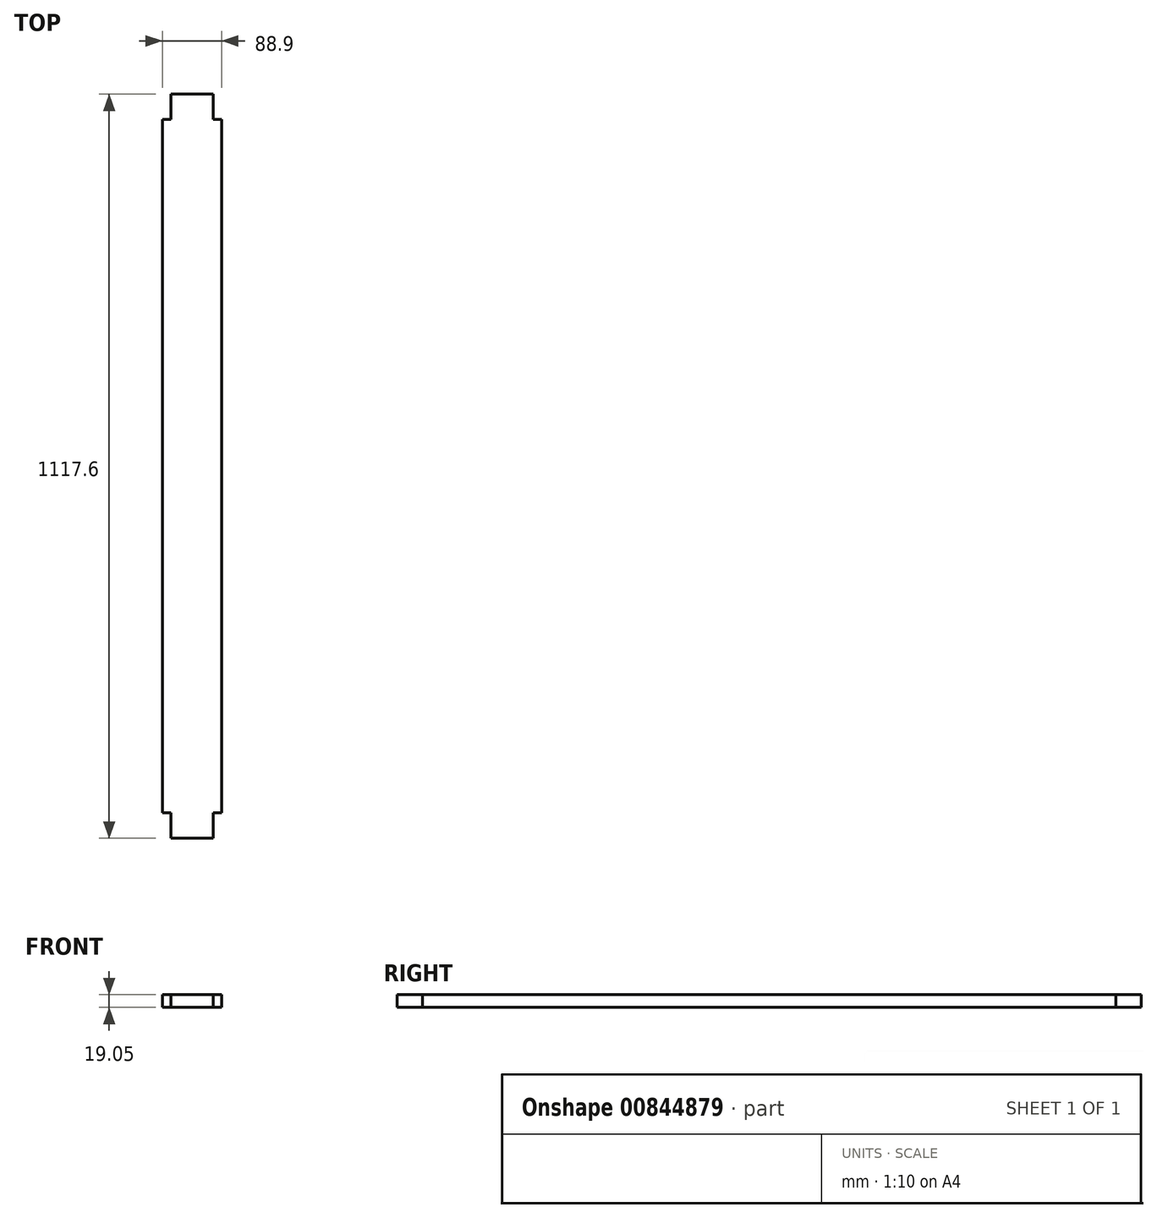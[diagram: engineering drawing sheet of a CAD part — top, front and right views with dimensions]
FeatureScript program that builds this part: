
annotation { "Feature Type Name" : "Feature", "Feature Type Description" : "" }
export const myFeature = defineFeature(function(context is Context, id is Id, definition is map)
    precondition{}
    {
        {
            var Q0;
            Q0=qCreatedBy(makeId("Front.planeOp"),FACE);
            var sketch = newSketch(context, id + "F0", { "sketchPlane" : qUnion([Q0])});
            skLineSegment(sketch, "E0.bottom", {"start": v(0, 0) * mm, "end": v(88.9, 0) * mm});
            skLineSegment(sketch, "E0.top", {"start": v(0, 19.05) * mm, "end": v(88.9, 19.05) * mm});
            skLineSegment(sketch, "E0.left", {"start": v(0, 0) * mm, "end": v(0, 19.05) * mm});
            skLineSegment(sketch, "E0.right", {"start": v(88.9, 0) * mm, "end": v(88.9, 19.05) * mm});
            skSolve(sketch);
        }
        {
            var Q0;
            Q0=makeQuery(id+"F0.imprint","IMPRINT",FACE,{"disambiguationData":[TD([[makeQuery(id+"F0.imprint","IMPRINT",EDGE,{"derivedFrom":sQuery(id+"F0.wireOp",EDGE,"E0.bottom")}),1.0]])]});
            extrude(context, id + "F1", {"entities" : qUnion([Q0]), "oppositeDirection" : true, "depth" : 1041.4 * mm, "offsetDistance" : 25.4 * mm});
        }
        {
            var Q0;
            Q0=makeQuery(id+"F1.opExtrude","CAP_FACE",FACE,{"disambiguationData":[OSD([sQuery(id+"F0.wireOp",EDGE,"E0.bottom"),sQuery(id+"F0.wireOp",EDGE,"E0.top"),sQuery(id+"F0.wireOp",EDGE,"E0.left"),sQuery(id+"F0.wireOp",EDGE,"E0.right")])],"isStart":true});
            var sketch = newSketch(context, id + "F2", { "sketchPlane" : qUnion([Q0])});
            skLineSegment(sketch, "E1.bottom", {"start": v(12.7, 0) * mm, "end": v(76.2, 0) * mm});
            skLineSegment(sketch, "E1.top", {"start": v(12.7, 19.05) * mm, "end": v(76.2, 19.05) * mm});
            skLineSegment(sketch, "E1.left", {"start": v(12.7, 0) * mm, "end": v(12.7, 19.05) * mm});
            skLineSegment(sketch, "E1.right", {"start": v(76.2, 0) * mm, "end": v(76.2, 19.05) * mm});
            skSolve(sketch);
        }
        {
            var Q0;
            Q0=makeQuery(id+"F2.imprint","IMPRINT",FACE,{"disambiguationData":[TD([[makeQuery(id+"F2.imprint","IMPRINT",EDGE,{"derivedFrom":sQuery(id+"F2.wireOp",EDGE,"E1.bottom")}),1.0]])]});
            extrude(context, id + "F3", {"entities" : qUnion([Q0]), "operationType" : NewBodyOperationType.ADD, "depth" : 38.1 * mm, "offsetDistance" : 25.4 * mm});
        }
        {
            var Q0;
            Q0=makeQuery(id+"F1.opExtrude","CAP_FACE",FACE,{"disambiguationData":[OSD([sQuery(id+"F0.wireOp",EDGE,"E0.bottom"),sQuery(id+"F0.wireOp",EDGE,"E0.top"),sQuery(id+"F0.wireOp",EDGE,"E0.left"),sQuery(id+"F0.wireOp",EDGE,"E0.right")])],"isStart":false});
            var sketch = newSketch(context, id + "F4", { "sketchPlane" : qUnion([Q0])});
            skLineSegment(sketch, "E2.bottom", {"start": v(-76.2, 19.05) * mm, "end": v(-12.7, 19.05) * mm});
            skLineSegment(sketch, "E2.top", {"start": v(-76.2, 0) * mm, "end": v(-12.7, 0) * mm});
            skLineSegment(sketch, "E2.left", {"start": v(-76.2, 19.05) * mm, "end": v(-76.2, 0) * mm});
            skLineSegment(sketch, "E2.right", {"start": v(-12.7, 19.05) * mm, "end": v(-12.7, 0) * mm});
            skSolve(sketch);
        }
        {
            var Q0;
            Q0=makeQuery(id+"F4.imprint","IMPRINT",FACE,{"disambiguationData":[TD([[makeQuery(id+"F4.imprint","IMPRINT",EDGE,{"derivedFrom":sQuery(id+"F4.wireOp",EDGE,"E2.bottom")}),1.0]])]});
            extrude(context, id + "F5", {"entities" : qUnion([Q0]), "operationType" : NewBodyOperationType.ADD, "depth" : 38.1 * mm, "offsetDistance" : 25.4 * mm});
        }
    });
